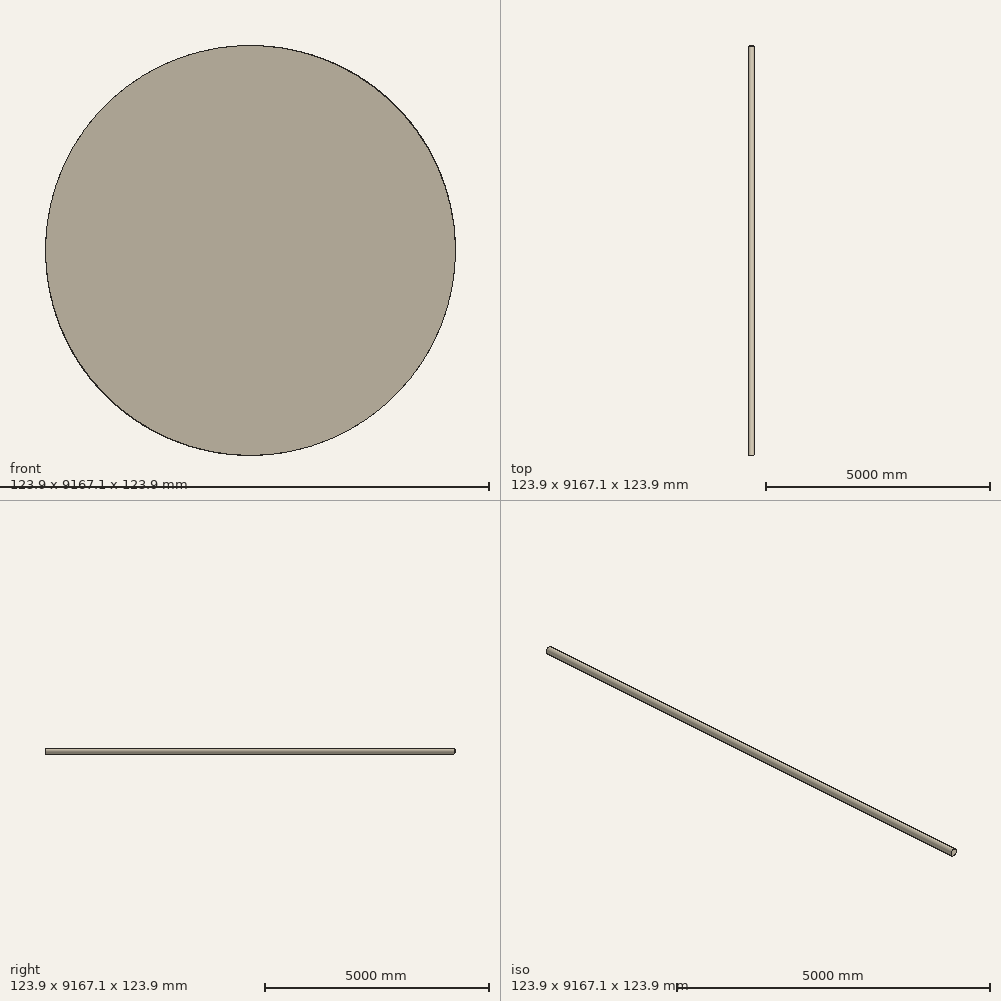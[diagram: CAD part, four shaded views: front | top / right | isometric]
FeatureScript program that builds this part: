
annotation { "Feature Type Name" : "Feature", "Feature Type Description" : "" }
export const myFeature = defineFeature(function(context is Context, id is Id, definition is map)
    precondition{}
    {
        {
            var Q0;
            Q0=qCreatedBy(makeId("Front.planeOp"),FACE);
            var sketch = newSketch(context, id + "F0", { "sketchPlane" : qUnion([Q0])});
            skCircle(sketch, "E0", {"center": v(0, 0) * mm, "radius": 61.97 * mm});
            skSolve(sketch);
        }
        {
            var Q0;
            Q0 = qSketchRegion(id + "F0", true);
            extrude(context, id + "F1", {"entities" : qUnion([Q0]), "endBound" : BoundingType.SYMMETRIC, "depth" : 9144 * mm, "offsetDistance" : 25.4 * mm});
        }
        {
            var Q0;
            Q0=makeQuery(id+"F1.opExtrude","CAP_FACE",FACE,{"disambiguationData":[OSD([sQuery(id+"F0.wireOp",EDGE,"E0")])],"isStart":true});
            cPlane(context, id + "F2", {"entities" : qUnion([Q0]), "cplaneType" : CPlaneType.OFFSET, "offset" : 23.1 * mm, "width" : 152.4 * mm, "height" : 152.4 * mm});
        }
        {
            var Q0;
            Q0=qCreatedBy(id+"F2.planeOp",FACE);
            var sketch = newSketch(context, id + "F3", { "sketchPlane" : qUnion([Q0])});
            skCircle(sketch, "E1", {"center": v(0, -13.73) * mm, "radius": 36.5 * mm});
            skSolve(sketch);
        }
        {
            var Q0;
            Q0=makeQuery(id+"F3.imprint","IMPRINT",FACE,{"disambiguationData":[TD([[makeQuery(id+"F3.imprint","IMPRINT",EDGE,{"derivedFrom":sQuery(id+"F3.wireOp",EDGE,"E1")}),1.0]])]});
            var Q1;
            Q1=makeQuery(id+"F1.opExtrude","CAP_FACE",FACE,{"disambiguationData":[OSD([sQuery(id+"F0.wireOp",EDGE,"E0")])],"isStart":true});
            loft(context, id + "F4", {"sheetProfilesArray" : [{ "sheetProfileEntities" : qUnion([Q0]) }, { "sheetProfileEntities" : qUnion([Q1]) }]});
        }
    });
